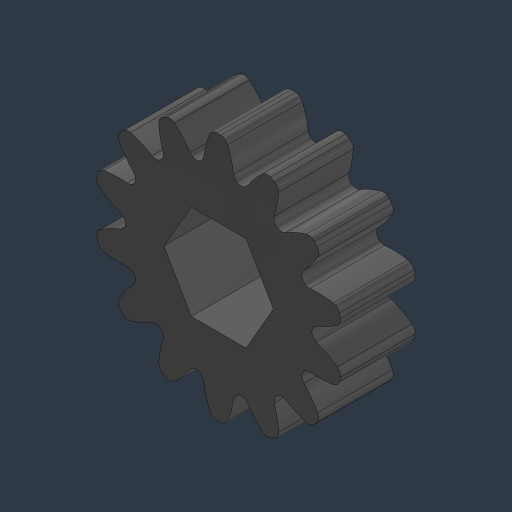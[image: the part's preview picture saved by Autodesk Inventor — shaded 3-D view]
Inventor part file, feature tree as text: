
AUTODESK INVENTOR PART (.ipt)
format: ipt  version: 2024.3 (Build 283343000, 343)  size: 312,832 bytes
history: native  units: mm (DEFAULTED — no unit token found)
features: plane x3, other x3, extrude x2, sketch x2, fillet x1, pattern_circular x1
ambient origin geometry x8: Origin, YZ Plane, XZ Plane, XY Plane, X Axis, Y Axis, Z Axis, Center Point
bodies: Solid1 (feature_tree)
feature tree (12):
  extrude  "Extrusion1"  Depth=10.0mm TaperAngle=0.0deg
  plane  "Work Plane2"
  plane  "Work Plane8"
  plane  "Work Plane9"
  other  "Spur Gear"
  extrude  "Extrusion2"  Depth=10.0mm TaperAngle=0.0deg
  fillet  "Fillet1"  Radius=29.6mm
  pattern_circular  "Circular Pattern1"  [2 undecoded]
  sketch  "Sketch1"  dims[d0=33.307842mm d1=10.0mm d2=0.0mm]
  other  "Srf1"
  sketch  "Sketch3"  dims[d3=28.0mm d4=10.0mm d5=0.0mm d16=29.6mm d17=0.0mm d34=2.243995mm d39=0.0mm d41=0.0mm d43=29.6mm d46=29.6mm d47=0.0mm d48=0.0mm d49=12.7mm d50=0.0mm d51=0.0mm d52=1.0mm d53=140.0mm d54=360.0deg]
  other  "Pitch Diameter"
note: 2 required parameter values undecoded (feature->parameter linkage not recoverable at this tier; creation-order binding heuristic only, values carry confidence <= 0.55)
